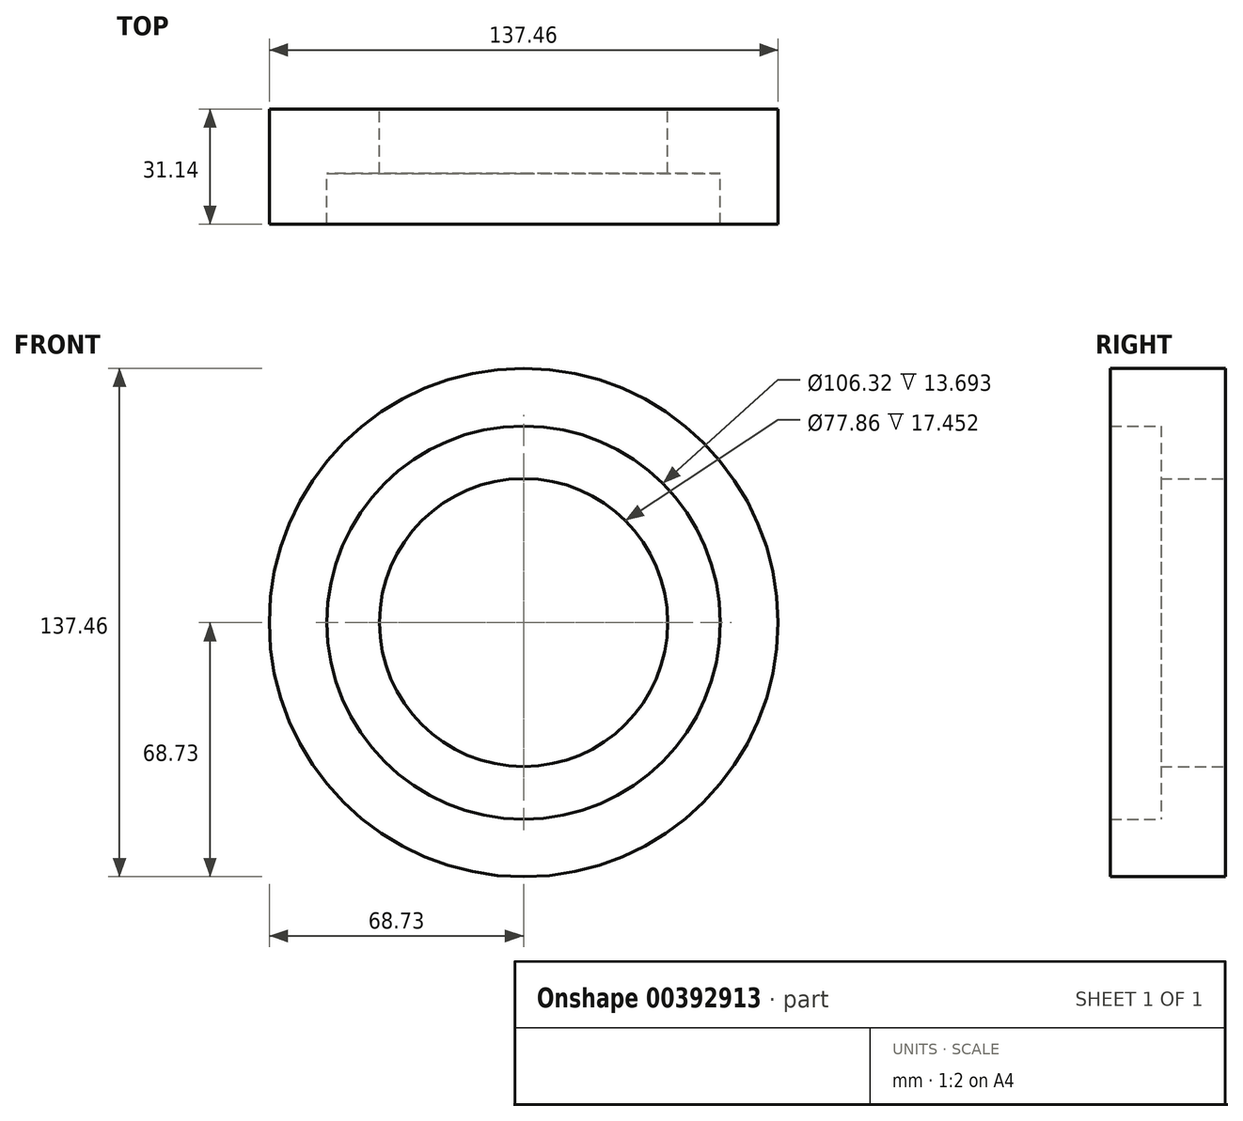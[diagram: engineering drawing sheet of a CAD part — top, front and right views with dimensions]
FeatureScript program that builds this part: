
annotation { "Feature Type Name" : "Feature", "Feature Type Description" : "" }
export const myFeature = defineFeature(function(context is Context, id is Id, definition is map)
    precondition{}
    {
        {
            var Q0;
            Q0=qCreatedBy(makeId("Top.planeOp"),FACE);
            var sketch = newSketch(context, id + "F0", { "sketchPlane" : qUnion([Q0])});
            skLineSegment(sketch, "E0.bottom", {"start": v(-68.73, 0) * mm, "end": v(-38.93, 0) * mm});
            skLineSegment(sketch, "E0.top", {"start": v(-68.73, -31.14) * mm, "end": v(-53.16, -31.14) * mm});
            skLineSegment(sketch, "E0.left", {"start": v(-68.73, 0) * mm, "end": v(-68.73, -31.14) * mm});
            skLineSegment(sketch, "E0.right", {"start": v(-38.93, 0) * mm, "end": v(-38.93, -17.45) * mm});
            skLineSegment(sketch, "E1.top", {"start": v(-38.93, -17.45) * mm, "end": v(-53.16, -17.45) * mm});
            skLineSegment(sketch, "E1.right", {"start": v(-53.16, -31.14) * mm, "end": v(-53.16, -17.45) * mm});
            skLineSegment(sketch, "E2", {"start": v(0, 0) * mm, "end": v(0, -34.37) * mm, "construction": true});
            skSolve(sketch);
        }
        {
            var Q0;
            Q0 = qSketchRegion(id + "F0", true);
            var Q1;
            Q1=sQuery(id+"F0.wireOp",EDGE,"E2");
            revolve(context, id + "F1", {"entities" : qUnion([Q0]), "axis" : qUnion([Q1]), "revolveType" : RevolveType.FULL});
        }
    });
